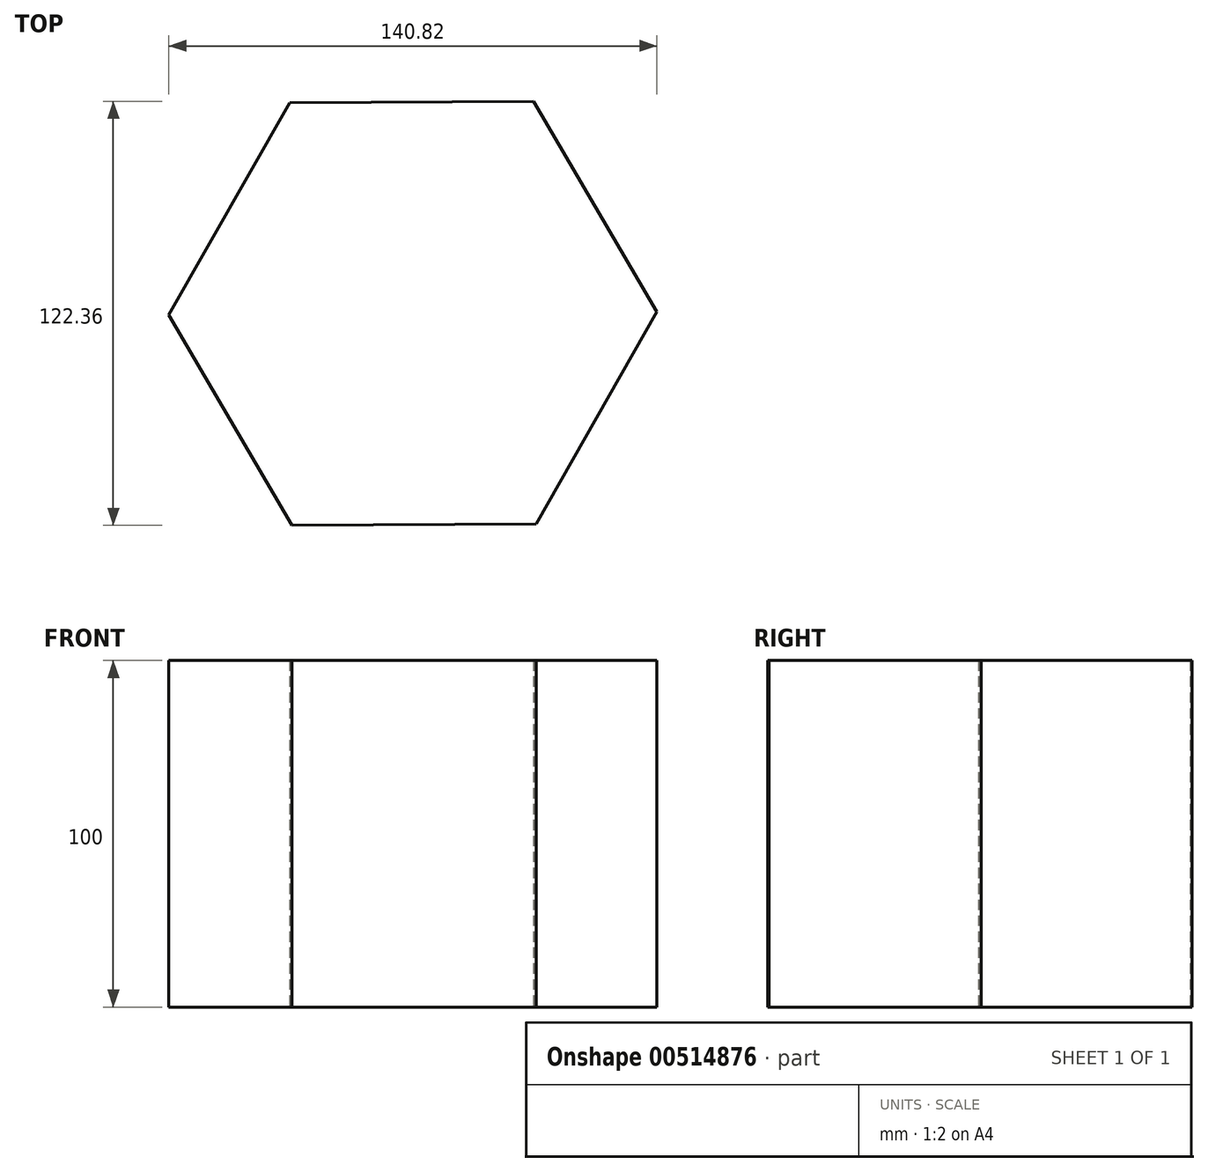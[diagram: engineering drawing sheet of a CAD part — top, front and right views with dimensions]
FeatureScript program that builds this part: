
annotation { "Feature Type Name" : "Feature", "Feature Type Description" : "" }
export const myFeature = defineFeature(function(context is Context, id is Id, definition is map)
    precondition{}
    {
        {
            var Q0;
            Q0=qCreatedBy(makeId("Top.planeOp"),FACE);
            var sketch = newSketch(context, id + "F0", { "sketchPlane" : qUnion([Q0])});
            skCircle(sketch, "E0.cCircle", {"center": v(0, 0) * mm, "radius": 70.41 * mm, "construction": true});
            skLineSegment(sketch, "E0.0", {"start": v(-35.56, 60.77) * mm, "end": v(34.85, 61.18) * mm});
            skLineSegment(sketch, "E0.1", {"start": v(34.85, 61.18) * mm, "end": v(70.41, 0.4) * mm});
            skLineSegment(sketch, "E0.2", {"start": v(70.41, 0.4) * mm, "end": v(35.56, -60.77) * mm});
            skLineSegment(sketch, "E0.3", {"start": v(35.56, -60.77) * mm, "end": v(-34.85, -61.18) * mm});
            skLineSegment(sketch, "E0.4", {"start": v(-34.85, -61.18) * mm, "end": v(-70.41, -0.4) * mm});
            skLineSegment(sketch, "E0.5", {"start": v(-70.41, -0.4) * mm, "end": v(-35.56, 60.77) * mm});
            skSolve(sketch);
        }
        {
            var Q0;
            Q0=makeQuery(id+"F0.imprint","IMPRINT",FACE,{"disambiguationData":[TD([[makeQuery(id+"F0.imprint","IMPRINT",EDGE,{"derivedFrom":sQuery(id+"F0.wireOp",EDGE,"E0.0")}),-1.0]])]});
            extrude(context, id + "F1", {"entities" : qUnion([Q0]), "depth" : 100 * mm, "offsetDistance" : 25.4 * mm});
        }
    });
